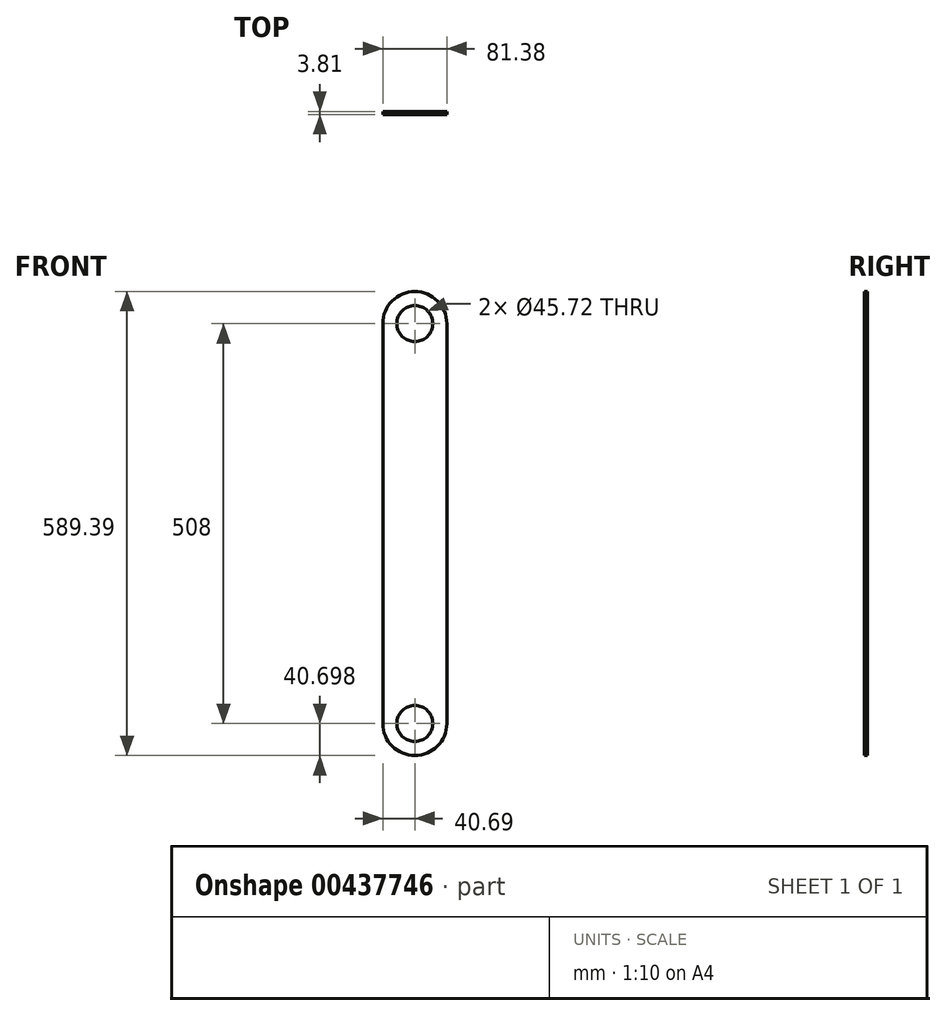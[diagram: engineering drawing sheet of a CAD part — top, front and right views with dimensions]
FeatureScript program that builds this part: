
annotation { "Feature Type Name" : "Feature", "Feature Type Description" : "" }
export const myFeature = defineFeature(function(context is Context, id is Id, definition is map)
    precondition{}
    {
        {
            var Q0;
            Q0=qCreatedBy(makeId("Front.planeOp"),FACE);
            var sketch = newSketch(context, id + "F0", { "sketchPlane" : qUnion([Q0])});
            skLineSegment(sketch, "E0", {"start": v(-64.64, -245.94) * mm, "end": v(-64.64, 262.06) * mm});
            skArc(sketch, "E1", {"start": v(16.74, 262.06) * mm, "mid": v(-23.95, 302.75) * mm, "end": v(-64.64, 262.06) * mm});
            skLineSegment(sketch, "E2", {"start": v(16.74, 262.06) * mm, "end": v(16.74, -245.94) * mm});
            skArc(sketch, "E3", {"start": v(-64.64, -245.94) * mm, "mid": v(-23.95, -286.64) * mm, "end": v(16.74, -245.94) * mm});
            skSolve(sketch);
        }
        {
            var Q0;
            Q0=makeQuery(id+"F0.imprint","IMPRINT",FACE,{"disambiguationData":[TD([[makeQuery(id+"F0.imprint","IMPRINT",EDGE,{"derivedFrom":sQuery(id+"F0.wireOp",EDGE,"E0")}),-1.0]])]});
            extrude(context, id + "F1", {"entities" : qUnion([Q0]), "depth" : 3.8 * mm});
        }
        {
            var Q0;
            Q0=makeQuery(id+"F1.opExtrude","CAP_FACE",FACE,{"disambiguationData":[OSD([sQuery(id+"F0.wireOp",EDGE,"E0"),sQuery(id+"F0.wireOp",EDGE,"E1"),sQuery(id+"F0.wireOp",EDGE,"E2"),sQuery(id+"F0.wireOp",EDGE,"E3")])],"isStart":false});
            var sketch = newSketch(context, id + "F2", { "sketchPlane" : qUnion([Q0])});
            skCircle(sketch, "E4", {"center": v(-23.95, 262.06) * mm, "radius": 22.86 * mm});
            skCircle(sketch, "E5", {"center": v(-23.95, -245.94) * mm, "radius": 22.86 * mm});
            skSolve(sketch);
        }
        {
            var Q0;
            Q0=makeQuery(id+"F2.imprint","IMPRINT",FACE,{"disambiguationData":[TD([[makeQuery(id+"F2.imprint","IMPRINT",EDGE,{"derivedFrom":sQuery(id+"F2.wireOp",EDGE,"E4")}),1.0]])]});
            var Q1;
            Q1=makeQuery(id+"F2.imprint","IMPRINT",FACE,{"disambiguationData":[TD([[makeQuery(id+"F2.imprint","IMPRINT",EDGE,{"derivedFrom":sQuery(id+"F2.wireOp",EDGE,"E5")}),1.0]])]});
            extrude(context, id + "F3", {"entities" : qUnion([Q0, Q1]), "operationType" : NewBodyOperationType.REMOVE, "oppositeDirection" : true, "depth" : 25.4 * mm});
        }
    });
